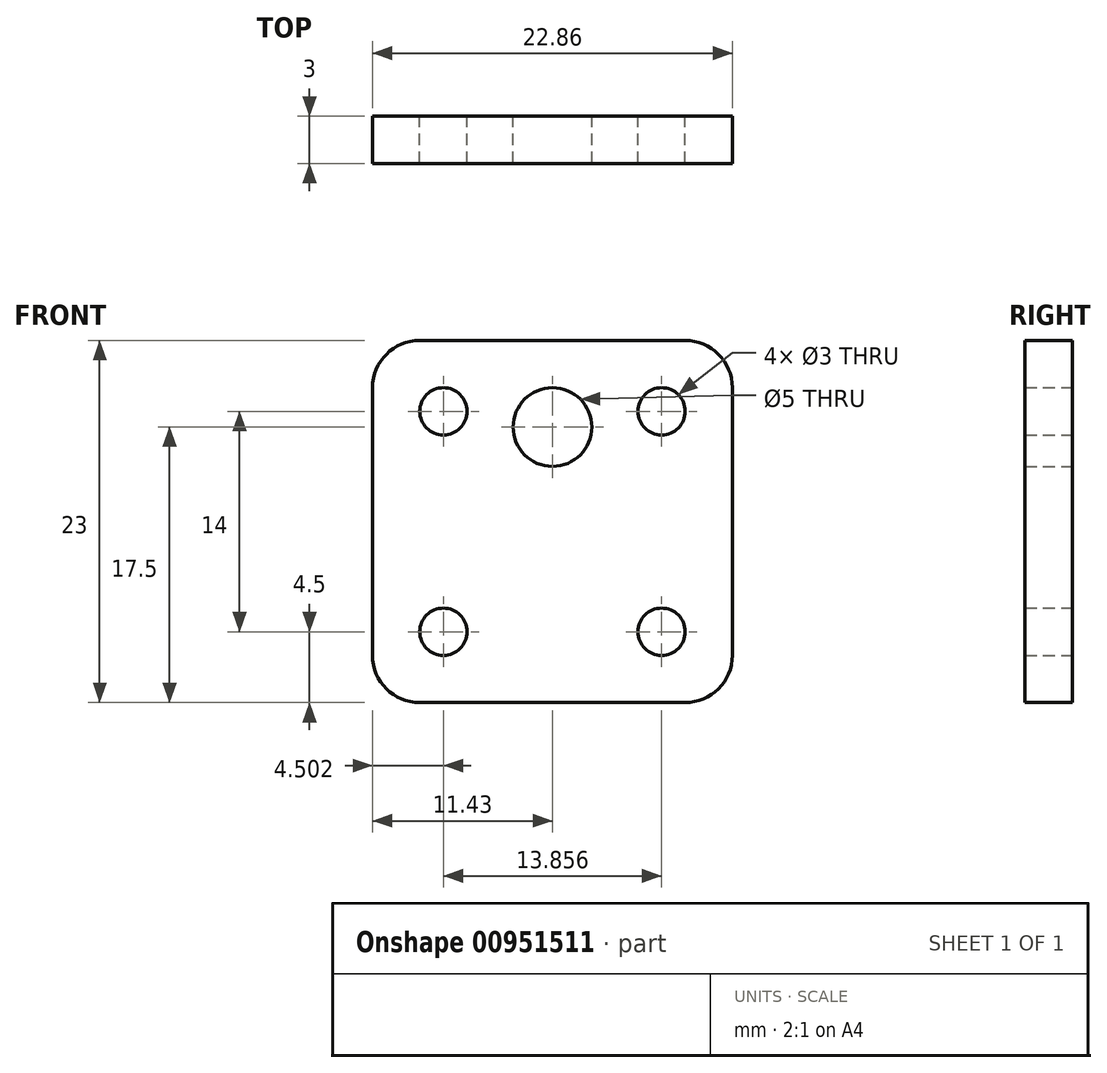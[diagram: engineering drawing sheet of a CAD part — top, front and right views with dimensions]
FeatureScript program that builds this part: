
annotation { "Feature Type Name" : "Feature", "Feature Type Description" : "" }
export const myFeature = defineFeature(function(context is Context, id is Id, definition is map)
    precondition{}
    {
        {
            var Q0;
            Q0=qCreatedBy(makeId("Front.planeOp"),FACE);
            var sketch = newSketch(context, id + "F0", { "sketchPlane" : qUnion([Q0])});
            skLineSegment(sketch, "E0.bottom", {"start": v(-8.43, -11.5) * mm, "end": v(8.43, -11.5) * mm});
            skLineSegment(sketch, "E0.top", {"start": v(-8.43, 11.5) * mm, "end": v(8.43, 11.5) * mm});
            skLineSegment(sketch, "E0.left", {"start": v(-11.43, -8.5) * mm, "end": v(-11.43, 8.5) * mm});
            skLineSegment(sketch, "E0.right", {"start": v(11.43, -8.5) * mm, "end": v(11.43, 8.5) * mm});
            skCircle(sketch, "E1", {"center": v(0, 6) * mm, "radius": 2.5 * mm});
            skCircle(sketch, "E2", {"center": v(6.93, 7) * mm, "radius": 1.5 * mm});
            skCircle(sketch, "E3", {"center": v(-6.93, 7) * mm, "radius": 1.5 * mm});
            skCircle(sketch, "E4", {"center": v(-6.93, -7) * mm, "radius": 1.5 * mm});
            skCircle(sketch, "E5", {"center": v(6.93, -7) * mm, "radius": 1.5 * mm});
            skPoint(sketch, "E6.visualSharp", {"position": v(11.43, 11.5) * mm});
            skArc(sketch, "E6.filletArc", {"start": v(11.43, 8.5) * mm, "mid": v(10.55, 10.62) * mm, "end": v(8.43, 11.5) * mm});
            skPoint(sketch, "E7.visualSharp", {"position": v(-11.43, 11.5) * mm});
            skArc(sketch, "E7.filletArc", {"start": v(-8.43, 11.5) * mm, "mid": v(-10.55, 10.62) * mm, "end": v(-11.43, 8.5) * mm});
            skPoint(sketch, "E8.visualSharp", {"position": v(-11.43, -11.5) * mm});
            skArc(sketch, "E8.filletArc", {"start": v(-11.43, -8.5) * mm, "mid": v(-10.55, -10.62) * mm, "end": v(-8.43, -11.5) * mm});
            skPoint(sketch, "E9.visualSharp", {"position": v(11.43, -11.5) * mm});
            skArc(sketch, "E9.filletArc", {"start": v(8.43, -11.5) * mm, "mid": v(10.55, -10.62) * mm, "end": v(11.43, -8.5) * mm});
            skSolve(sketch);
        }
        {
            var Q0;
            Q0=qSketchRegion(id+"F0",true);
            extrude(context, id + "F1", {"entities" : qUnion([Q0]), "depth" : 3 * mm, "offsetDistance" : 25 * mm});
        }
    });
